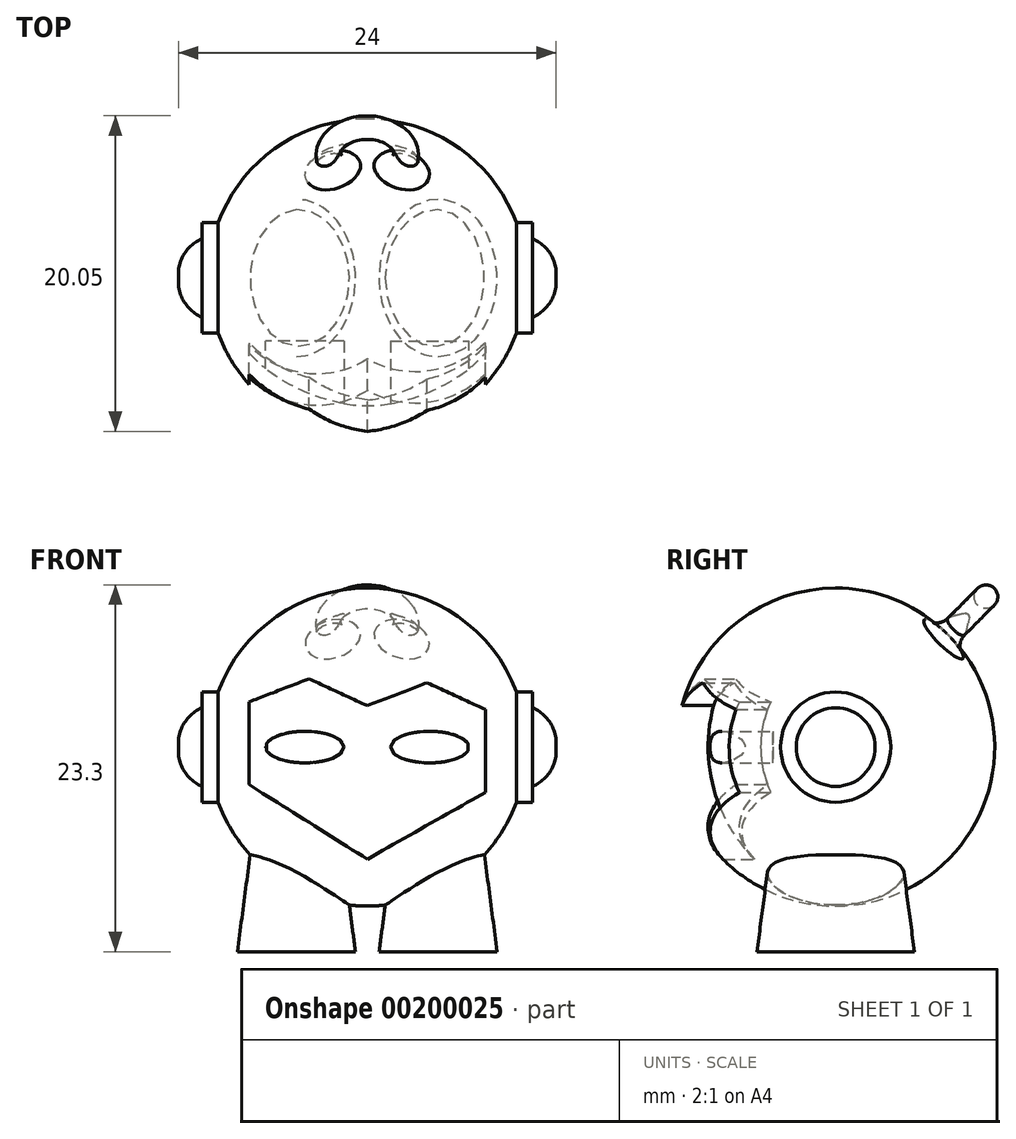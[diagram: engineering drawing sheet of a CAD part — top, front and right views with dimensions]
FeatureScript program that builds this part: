
annotation { "Feature Type Name" : "Feature", "Feature Type Description" : "" }
export const myFeature = defineFeature(function(context is Context, id is Id, definition is map)
    precondition{}
    {
        {
            var Q0;
            Q0=qCreatedBy(makeId("Top.planeOp"),FACE);
            var sketch = newSketch(context, id + "F0", { "sketchPlane" : qUnion([Q0])});
            skCircle(sketch, "E0", {"center": v(0, 0) * mm, "radius": 10.1 * mm});
            skSolve(sketch);
        }
        {
            var Q0;
            Q0 = qSketchRegion(id + "F0", true);
            extrude(context, id + "F1", {"entities" : qUnion([Q0]), "endBound" : BoundingType.SYMMETRIC, "depth" : 20.2 * mm});
        }
        {
            var Q0;
            Q0=makeQuery(id+"F1.opExtrude","CAP_EDGE",EDGE,{"disambiguationData":[OSD([sQuery(id+"F0.wireOp",EDGE,"E0")])],"isStart":false});
            var Q1;
            Q1=makeQuery(id+"F1.opExtrude","CAP_EDGE",EDGE,{"disambiguationData":[OSD([sQuery(id+"F0.wireOp",EDGE,"E0")])],"isStart":true});
            fillet(context, id + "F2", {"entities" : qUnion([Q0, Q1]), "radius" : 10.1 * mm, "tangentPropagation" : true, "allowEdgeOverflow" : false});
        }
        {
            var Q0;
            Q0=qCreatedBy(makeId("Top.planeOp"),FACE);
            cPlane(context, id + "F3", {"entities" : qUnion([Q0]), "cplaneType" : CPlaneType.OFFSET, "offset" : 13 * mm, "oppositeDirection" : true, "width" : 150 * mm, "height" : 150 * mm});
        }
        {
            var Q0;
            Q0=qCreatedBy(id+"F3.planeOp",FACE);
            var sketch = newSketch(context, id + "F4", { "sketchPlane" : qUnion([Q0])});
            skEllipse(sketch, "E1", {"center": v(-4.5, 0) * mm, "majorRadius": 5 * mm, "minorRadius": 3.75 * mm, "majorAxis": v(0, 1)});
            skEllipse(sketch, "E2", {"center": v(4.5, 0) * mm, "majorRadius": 5 * mm, "minorRadius": 3.75 * mm, "majorAxis": v(0, 1)});
            skLineSegment(sketch, "E3", {"start": v(-4.5, 0) * mm, "end": v(4.5, 0) * mm, "construction": true});
            skLineSegment(sketch, "E4", {"start": v(-4.5, 0) * mm, "end": v(0, 0) * mm, "construction": true});
            skSolve(sketch);
        }
        {
            var Q0;
            Q0=makeQuery(id+"F4.imprint","IMPRINT",FACE,{"disambiguationData":[TD([[makeQuery(id+"F4.imprint","IMPRINT",EDGE,{"derivedFrom":sQuery(id+"F4.wireOp",EDGE,"E1")}),1.0]])]});
            var Q1;
            Q1=makeQuery(id+"F4.imprint","IMPRINT",FACE,{"disambiguationData":[TD([[makeQuery(id+"F4.imprint","IMPRINT",EDGE,{"derivedFrom":sQuery(id+"F4.wireOp",EDGE,"E2")}),1.0]])]});
            extrude(context, id + "F5", {"entities" : qUnion([Q0, Q1]), "operationType" : NewBodyOperationType.ADD, "depth" : 10 * mm, "hasDraft" : true, "draftAngle" : 7.5 * degree, "draftPullDirection" : true});
        }
        {
            var Q0;
            Q0=qCreatedBy(makeId("Front.planeOp"),FACE);
            cPlane(context, id + "F6", {"entities" : qUnion([Q0]), "cplaneType" : CPlaneType.OFFSET, "offset" : 11 * mm, "width" : 150 * mm, "height" : 150 * mm});
        }
        {
            var Q0;
            Q0=qCreatedBy(id+"F6.planeOp",FACE);
            var sketch = newSketch(context, id + "F7", { "sketchPlane" : qUnion([Q0])});
            skLineSegment(sketch, "E5.left", {"start": v(7.5, 2.39) * mm, "end": v(7.5, -2.88) * mm});
            skLineSegment(sketch, "E5.right", {"start": v(-7.5, 2.88) * mm, "end": v(-7.5, -2.39) * mm});
            skPoint(sketch, "E5.middle", {"position": v(0, 0) * mm});
            skLineSegment(sketch, "E6", {"start": v(0, 2.63) * mm, "end": v(-3.7, 4.33) * mm});
            skLineSegment(sketch, "E7", {"start": v(-3.7, 4.33) * mm, "end": v(-7.5, 2.88) * mm});
            skLineSegment(sketch, "E8", {"start": v(0, 2.63) * mm, "end": v(3.8, 4.09) * mm});
            skLineSegment(sketch, "E9", {"start": v(3.8, 4.09) * mm, "end": v(7.5, 2.39) * mm});
            skLineSegment(sketch, "E10", {"start": v(7.5, -2.88) * mm, "end": v(0, -7.12) * mm});
            skLineSegment(sketch, "E11", {"start": v(0, -7.12) * mm, "end": v(-7.5, -2.39) * mm});
            skSolve(sketch);
        }
        {
            var Q0;
            Q0=makeQuery(id+"F7.imprint","IMPRINT",FACE,{"disambiguationData":[TD([[makeQuery(id+"F7.imprint","IMPRINT",EDGE,{"derivedFrom":sQuery(id+"F7.wireOp",EDGE,"E5.left")}),-1.0]])]});
            extrude(context, id + "F8", {"entities" : qUnion([Q0]), "depth" : 10 * mm});
        }
        {
            var Q0;
            Q0=makeQuery(id+"F8.opExtrude","SWEPT_BODY",BODY,{"disambiguationData":[OSD([sQuery(id+"F7.wireOp",EDGE,"E5.left"),sQuery(id+"F7.wireOp",EDGE,"E5.right"),sQuery(id+"F7.wireOp",EDGE,"E6"),sQuery(id+"F7.wireOp",EDGE,"E7"),sQuery(id+"F7.wireOp",EDGE,"E8"),sQuery(id+"F7.wireOp",EDGE,"E9"),sQuery(id+"F7.wireOp",EDGE,"E10"),sQuery(id+"F7.wireOp",EDGE,"E11")])]});
            transform(context, id + "F9", {"entities" : qUnion([Q0]), "transformType" : TransformType.TRANSLATION_3D, "dx" : 0 * mm, "dy" : 5 * mm, "dz" : 0 * mm, "makeCopy" : false});
        }
        {
            var Q0;
            Q0=makeQuery(id+"F1.opExtrude","SWEPT_BODY",BODY,{"disambiguationData":[OSD([sQuery(id+"F0.wireOp",EDGE,"E0")])]});
            var Q1;
            Q1=makeQuery(id+"F8.opExtrude","SWEPT_BODY",BODY,{"disambiguationData":[OSD([sQuery(id+"F7.wireOp",EDGE,"E5.left"),sQuery(id+"F7.wireOp",EDGE,"E5.right"),sQuery(id+"F7.wireOp",EDGE,"E6"),sQuery(id+"F7.wireOp",EDGE,"E7"),sQuery(id+"F7.wireOp",EDGE,"E8"),sQuery(id+"F7.wireOp",EDGE,"E9"),sQuery(id+"F7.wireOp",EDGE,"E10"),sQuery(id+"F7.wireOp",EDGE,"E11")])]});
            booleanBodies(context, id + "F10", {"operationType" : BooleanOperationType.SUBTRACTION, "tools" : qUnion([Q0]), "targets" : qUnion([Q1]), "keepTools" : true});
        }
        {
            var Q0;
            Q0=makeQuery(id+"F8.opExtrude","SWEPT_BODY",BODY,{"disambiguationData":[OSD([sQuery(id+"F7.wireOp",EDGE,"E5.left"),sQuery(id+"F7.wireOp",EDGE,"E5.right"),sQuery(id+"F7.wireOp",EDGE,"E6"),sQuery(id+"F7.wireOp",EDGE,"E7"),sQuery(id+"F7.wireOp",EDGE,"E8"),sQuery(id+"F7.wireOp",EDGE,"E9"),sQuery(id+"F7.wireOp",EDGE,"E10"),sQuery(id+"F7.wireOp",EDGE,"E11")])]});
            transform(context, id + "F11", {"entities" : qUnion([Q0]), "transformType" : TransformType.TRANSLATION_3D, "dx" : 0 * mm, "dy" : 2 * mm, "dz" : 0 * mm, "makeCopy" : false});
        }
        {
            var Q0;
            Q0=makeQuery(id+"F8.opExtrude","SWEPT_BODY",BODY,{"disambiguationData":[OSD([sQuery(id+"F7.wireOp",EDGE,"E5.left"),sQuery(id+"F7.wireOp",EDGE,"E5.right"),sQuery(id+"F7.wireOp",EDGE,"E6"),sQuery(id+"F7.wireOp",EDGE,"E7"),sQuery(id+"F7.wireOp",EDGE,"E8"),sQuery(id+"F7.wireOp",EDGE,"E9"),sQuery(id+"F7.wireOp",EDGE,"E10"),sQuery(id+"F7.wireOp",EDGE,"E11")])]});
            var Q1;
            Q1=makeQuery(id+"F1.opExtrude","SWEPT_BODY",BODY,{"disambiguationData":[OSD([sQuery(id+"F0.wireOp",EDGE,"E0")])]});
            booleanBodies(context, id + "F12", {"operationType" : BooleanOperationType.SUBTRACTION, "tools" : qUnion([Q0]), "targets" : qUnion([Q1])});
        }
        {
            var Q0;
            Q0=qCreatedBy(id+"F6.planeOp",FACE);
            var sketch = newSketch(context, id + "F13", { "sketchPlane" : qUnion([Q0])});
            skEllipse(sketch, "E12", {"center": v(-3.96, 0) * mm, "majorRadius": 2.5 * mm, "minorRadius": 1 * mm, "majorAxis": v(1, 0)});
            skLineSegment(sketch, "E13", {"start": v(0, -1.85) * mm, "end": v(0, 0.8) * mm, "construction": true});
            skEllipse(sketch, "E14.MirrorC", {"center": v(3.96, 0) * mm, "majorRadius": 2.5 * mm, "minorRadius": 1 * mm, "majorAxis": v(-1, 0)});
            skSolve(sketch);
        }
        {
            var Q0;
            Q0=makeQuery(id+"F13.imprint","IMPRINT",FACE,{"disambiguationData":[TD([[makeQuery(id+"F13.imprint","IMPRINT",EDGE,{"derivedFrom":sQuery(id+"F13.wireOp",EDGE,"E12")}),1.0]])]});
            var Q1;
            Q1=makeQuery(id+"F13.imprint","IMPRINT",FACE,{"disambiguationData":[TD([[makeQuery(id+"F13.imprint","IMPRINT",EDGE,{"derivedFrom":sQuery(id+"F13.wireOp",EDGE,"E14.MirrorC")}),1.0]])]});
            extrude(context, id + "F14", {"entities" : qUnion([Q0, Q1]), "oppositeDirection" : true, "depth" : 7 * mm});
        }
        {
            var Q0;
            Q0=makeQuery(id+"F14.opExtrude","SWEPT_BODY",BODY,{"disambiguationData":[OSD([sQuery(id+"F13.wireOp",EDGE,"E12")])]});
            var Q1;
            Q1=makeQuery(id+"F14.opExtrude","SWEPT_BODY",BODY,{"disambiguationData":[OSD([sQuery(id+"F13.wireOp",EDGE,"E14.MirrorC")])]});
            var Q2;
            Q2=makeQuery(id+"F1.opExtrude","SWEPT_BODY",BODY,{"disambiguationData":[OSD([sQuery(id+"F0.wireOp",EDGE,"E0")])]});
            booleanBodies(context, id + "F15", {"operationType" : BooleanOperationType.SUBTRACTION, "tools" : qUnion([Q0, Q1]), "targets" : qUnion([Q2])});
        }
        {
            var Q0;
            Q0=qCreatedBy(makeId("Right.planeOp"),FACE);
            var sketch = newSketch(context, id + "F16", { "sketchPlane" : qUnion([Q0])});
            skCircle(sketch, "E15", {"center": v(0, 0) * mm, "radius": 3.5 * mm});
            skCircle(sketch, "E16", {"center": v(0, 0) * mm, "radius": 2.5 * mm});
            skSolve(sketch);
        }
        {
            var Q0;
            Q0=makeQuery(id+"F16.imprint","IMPRINT",FACE,{"disambiguationData":[TD([[makeQuery(id+"F16.imprint","IMPRINT",EDGE,{"derivedFrom":sQuery(id+"F16.wireOp",EDGE,"E15")}),1.0]])]});
            extrude(context, id + "F17", {"entities" : qUnion([Q0]), "operationType" : NewBodyOperationType.ADD, "endBound" : BoundingType.SYMMETRIC, "depth" : 21 * mm});
        }
        {
            var Q0;
            Q0=makeQuery(id+"F16.imprint","IMPRINT",FACE,{"disambiguationData":[TD([[makeQuery(id+"F16.imprint","IMPRINT",EDGE,{"derivedFrom":sQuery(id+"F16.wireOp",EDGE,"E16")}),1.0]])]});
            extrude(context, id + "F18", {"entities" : qUnion([Q0]), "operationType" : NewBodyOperationType.ADD, "endBound" : BoundingType.SYMMETRIC, "depth" : 24 * mm});
        }
        {
            var Q0;
            Q0=makeQuery(id+"F18.opExtrude","CAP_EDGE",EDGE,{"disambiguationData":[OSD([sQuery(id+"F16.wireOp",EDGE,"E16")])],"isStart":true});
            var Q1;
            Q1=makeQuery(id+"F18.opExtrude","CAP_EDGE",EDGE,{"disambiguationData":[OSD([sQuery(id+"F16.wireOp",EDGE,"E16")])],"isStart":false});
            fillet(context, id + "F19", {"entities" : qUnion([Q0, Q1]), "radius" : 2.5 * mm, "tangentPropagation" : true, "allowEdgeOverflow" : false});
        }
        {
            var Q0;
            Q0=qCreatedBy(id+"F3.planeOp",FACE);
            var sketch = newSketch(context, id + "F20", { "sketchPlane" : qUnion([Q0])});
            skArc(sketch, "E17", {"start": v(2.5, 0) * mm, "mid": v(0, 2.5) * mm, "end": v(-2.5, 0) * mm});
            skLineSegment(sketch, "E18", {"start": v(-2.5, 0) * mm, "end": v(2.5, 0) * mm, "construction": true});
            skCircle(sketch, "E19", {"center": v(0, 0) * mm, "radius": 2.5 * mm});
            skSolve(sketch);
        }
        {
            var Q0;
            Q0=qCreatedBy(makeId("Front.planeOp"),FACE);
            var sketch = newSketch(context, id + "F21", { "sketchPlane" : qUnion([Q0])});
            skCircle(sketch, "E20", {"center": v(-2.5, -13) * mm, "radius": 0.75 * mm});
            skSolve(sketch);
        }
        {
            var Q0;
            Q0=makeQuery(id+"F21.imprint","IMPRINT",FACE,{"disambiguationData":[TD([[makeQuery(id+"F21.imprint","IMPRINT",EDGE,{"derivedFrom":sQuery(id+"F21.wireOp",EDGE,"E20")}),1.0]])]});
            var Q1;
            Q1=sQuery(id+"F20.wireOp",EDGE,"E19");
            sweep(context, id + "F22", {"profiles" : qUnion([Q0]), "path" : qUnion([Q1])});
        }
        {
            var Q0;
            Q0=makeQuery(id+"F22.opSweep","SWEPT_BODY",BODY,{"disambiguationData":[OSD([sQuery(id+"F20.wireOp",EDGE,"E17"),sQuery(id+"F21.wireOp",EDGE,"E20")])]});
            transform(context, id + "F23", {"entities" : qUnion([Q0]), "transformType" : TransformType.TRANSLATION_3D, "dx" : 0 * mm, "dy" : 11 * mm, "dz" : 13 * mm, "makeCopy" : false});
        }
        {
            var Q0;
            Q0=makeQuery(id+"F22.opSweep","SWEPT_BODY",BODY,{"disambiguationData":[OSD([sQuery(id+"F20.wireOp",EDGE,"E17"),sQuery(id+"F21.wireOp",EDGE,"E20")])]});
            var Q1;
            Q1=makeQuery(id+"F17.opExtrude","CAP_EDGE",EDGE,{"disambiguationData":[OSD([sQuery(id+"F16.wireOp",EDGE,"E15")])],"isStart":true});
            transform(context, id + "F24", {"entities" : qUnion([Q0]), "transformType" : TransformType.ROTATION, "transformAxis" : qUnion([Q1]), "angle" : 45 * degree, "makeCopy" : false});
        }
        {
            var Q0;
            Q0=makeQuery(id+"F1.opExtrude","SWEPT_BODY",BODY,{"disambiguationData":[OSD([sQuery(id+"F0.wireOp",EDGE,"E0")])]});
            var Q1;
            Q1=makeQuery(id+"F22.opSweep","SWEPT_BODY",BODY,{"disambiguationData":[OSD([sQuery(id+"F20.wireOp",EDGE,"E19"),sQuery(id+"F21.wireOp",EDGE,"E20")])]});
            booleanBodies(context, id + "F25", {"operationType" : BooleanOperationType.UNION, "tools" : qUnion([Q0, Q1])});
        }
        {
            var Q0;
            Q0=makeQuery(id+"F25.opBoolean","INTERSECT",EDGE,{"disambiguationData":[OD(0.0)],"derivedFrom":[makeQuery(id+"F17.boolean.opBoolean","SPLIT",FACE,{"disambiguationData":[TD([makeQuery(id+"F5.opExtrude","SWEPT_FACE",FACE,{"disambiguationData":[OSD([sQuery(id+"F4.wireOp",EDGE,"E1")])]}),makeQuery(id+"F5.opExtrude","SWEPT_FACE",FACE,{"disambiguationData":[OSD([sQuery(id+"F4.wireOp",EDGE,"E2")])]}),makeQuery(id+"F12.opBoolean","COPY",FACE,{"derivedFrom":makeQuery(id+"F8.opExtrude","SWEPT_FACE",FACE,{"disambiguationData":[OSD([sQuery(id+"F7.wireOp",EDGE,"E5.left")])]})}),makeQuery(id+"F12.opBoolean","COPY",FACE,{"derivedFrom":makeQuery(id+"F8.opExtrude","SWEPT_FACE",FACE,{"disambiguationData":[OSD([sQuery(id+"F7.wireOp",EDGE,"E5.right")])]})}),makeQuery(id+"F12.opBoolean","COPY",FACE,{"derivedFrom":makeQuery(id+"F8.opExtrude","SWEPT_FACE",FACE,{"disambiguationData":[OSD([sQuery(id+"F7.wireOp",EDGE,"E6")])]})}),makeQuery(id+"F12.opBoolean","COPY",FACE,{"derivedFrom":makeQuery(id+"F8.opExtrude","SWEPT_FACE",FACE,{"disambiguationData":[OSD([sQuery(id+"F7.wireOp",EDGE,"E7")])]})}),makeQuery(id+"F12.opBoolean","COPY",FACE,{"derivedFrom":makeQuery(id+"F8.opExtrude","SWEPT_FACE",FACE,{"disambiguationData":[OSD([sQuery(id+"F7.wireOp",EDGE,"E8")])]})}),makeQuery(id+"F12.opBoolean","COPY",FACE,{"derivedFrom":makeQuery(id+"F8.opExtrude","SWEPT_FACE",FACE,{"disambiguationData":[OSD([sQuery(id+"F7.wireOp",EDGE,"E9")])]})}),makeQuery(id+"F12.opBoolean","COPY",FACE,{"derivedFrom":makeQuery(id+"F8.opExtrude","SWEPT_FACE",FACE,{"disambiguationData":[OSD([sQuery(id+"F7.wireOp",EDGE,"E10")])]})}),makeQuery(id+"F12.opBoolean","COPY",FACE,{"derivedFrom":makeQuery(id+"F8.opExtrude","SWEPT_FACE",FACE,{"disambiguationData":[OSD([sQuery(id+"F7.wireOp",EDGE,"E11")])]})}),makeQuery(id+"F17.opExtrude","SWEPT_FACE",FACE,{"disambiguationData":[OSD([sQuery(id+"F16.wireOp",EDGE,"E15")])]})])],"derivedFrom":makeQuery(id+"F2.opFillet","BLEND_FACE",FACE,{"disambiguationData":[OSD([sQuery(id+"F0.wireOp",EDGE,"E0")])]})}),makeQuery(id+"F22.opSweep","SWEPT_FACE",FACE,{"disambiguationData":[OSD([sQuery(id+"F20.wireOp",EDGE,"E19"),sQuery(id+"F21.wireOp",EDGE,"E20")])]})]});
            var Q1;
            Q1=makeQuery(id+"F25.opBoolean","INTERSECT",EDGE,{"disambiguationData":[OD(1.0)],"derivedFrom":[makeQuery(id+"F17.boolean.opBoolean","SPLIT",FACE,{"disambiguationData":[TD([makeQuery(id+"F5.opExtrude","SWEPT_FACE",FACE,{"disambiguationData":[OSD([sQuery(id+"F4.wireOp",EDGE,"E1")])]}),makeQuery(id+"F5.opExtrude","SWEPT_FACE",FACE,{"disambiguationData":[OSD([sQuery(id+"F4.wireOp",EDGE,"E2")])]}),makeQuery(id+"F12.opBoolean","COPY",FACE,{"derivedFrom":makeQuery(id+"F8.opExtrude","SWEPT_FACE",FACE,{"disambiguationData":[OSD([sQuery(id+"F7.wireOp",EDGE,"E5.left")])]})}),makeQuery(id+"F12.opBoolean","COPY",FACE,{"derivedFrom":makeQuery(id+"F8.opExtrude","SWEPT_FACE",FACE,{"disambiguationData":[OSD([sQuery(id+"F7.wireOp",EDGE,"E5.right")])]})}),makeQuery(id+"F12.opBoolean","COPY",FACE,{"derivedFrom":makeQuery(id+"F8.opExtrude","SWEPT_FACE",FACE,{"disambiguationData":[OSD([sQuery(id+"F7.wireOp",EDGE,"E6")])]})}),makeQuery(id+"F12.opBoolean","COPY",FACE,{"derivedFrom":makeQuery(id+"F8.opExtrude","SWEPT_FACE",FACE,{"disambiguationData":[OSD([sQuery(id+"F7.wireOp",EDGE,"E7")])]})}),makeQuery(id+"F12.opBoolean","COPY",FACE,{"derivedFrom":makeQuery(id+"F8.opExtrude","SWEPT_FACE",FACE,{"disambiguationData":[OSD([sQuery(id+"F7.wireOp",EDGE,"E8")])]})}),makeQuery(id+"F12.opBoolean","COPY",FACE,{"derivedFrom":makeQuery(id+"F8.opExtrude","SWEPT_FACE",FACE,{"disambiguationData":[OSD([sQuery(id+"F7.wireOp",EDGE,"E9")])]})}),makeQuery(id+"F12.opBoolean","COPY",FACE,{"derivedFrom":makeQuery(id+"F8.opExtrude","SWEPT_FACE",FACE,{"disambiguationData":[OSD([sQuery(id+"F7.wireOp",EDGE,"E10")])]})}),makeQuery(id+"F12.opBoolean","COPY",FACE,{"derivedFrom":makeQuery(id+"F8.opExtrude","SWEPT_FACE",FACE,{"disambiguationData":[OSD([sQuery(id+"F7.wireOp",EDGE,"E11")])]})}),makeQuery(id+"F17.opExtrude","SWEPT_FACE",FACE,{"disambiguationData":[OSD([sQuery(id+"F16.wireOp",EDGE,"E15")])]})])],"derivedFrom":makeQuery(id+"F2.opFillet","BLEND_FACE",FACE,{"disambiguationData":[OSD([sQuery(id+"F0.wireOp",EDGE,"E0")])]})}),makeQuery(id+"F22.opSweep","SWEPT_FACE",FACE,{"disambiguationData":[OSD([sQuery(id+"F20.wireOp",EDGE,"E19"),sQuery(id+"F21.wireOp",EDGE,"E20")])]})]});
            fillet(context, id + "F26", {"entities" : qUnion([Q0, Q1]), "radius" : 1.2 * mm, "tangentPropagation" : true, "allowEdgeOverflow" : false});
        }
    });
